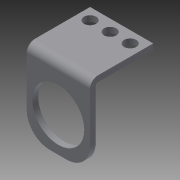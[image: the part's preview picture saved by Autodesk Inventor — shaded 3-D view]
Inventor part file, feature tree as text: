
AUTODESK INVENTOR PART (.ipt)
format: ipt  version: 2013 (Build 170138000, 138)  size: 198,144 bytes
history: native  units: in
note: dims shown in document units (in); Inventor stores cm internally (conversion verified against a paired STEP export)
features: other x5, sheet_metal_op x4, sketch x4
ambient origin geometry x8: Origin, YZ Plane, XZ Plane, XY Plane, X Axis, Y Axis, Z Axis, Center Point
bodies: Solid1 (feature_tree)
feature tree (13):
  sheet_metal_op  "Face1"
  sheet_metal_op  "Flange1"
  sketch  "Sketch1"  dims[d0=1.3714in]
  other  "Plate1"
  sketch  "Sketch4"  dims[d2=1.25in]
  other  "Plate3"
  sheet_metal_op  "Bend2"
  sheet_metal_op  "Corner1"
  sketch  "Sketch5"  dims[d3=0.266in]
  sketch  "Sketch6"  dims[d4=0.266in d5=0.4357in d6=0.266in d7=0.4357in d8=0.25in d9=0.25in d10=0.25in d11=0.25in d12=0.125in d28=0.125in d29=0.0625in d30=0.25in d31=0.125in d32=1.75in d33=90.0deg d34=0.05in d35=0.5in d36=0.125in d37=0.125in d38=1.125in d39=0.125in d40=0.0in d41=0.75in d43=0.0in d44=1.0in d47=1.0in d48=0.125in d49=0.0in d1=0.125in]
  other  "Cut1"
  other  "Cut2"
  other  "Definition1"
